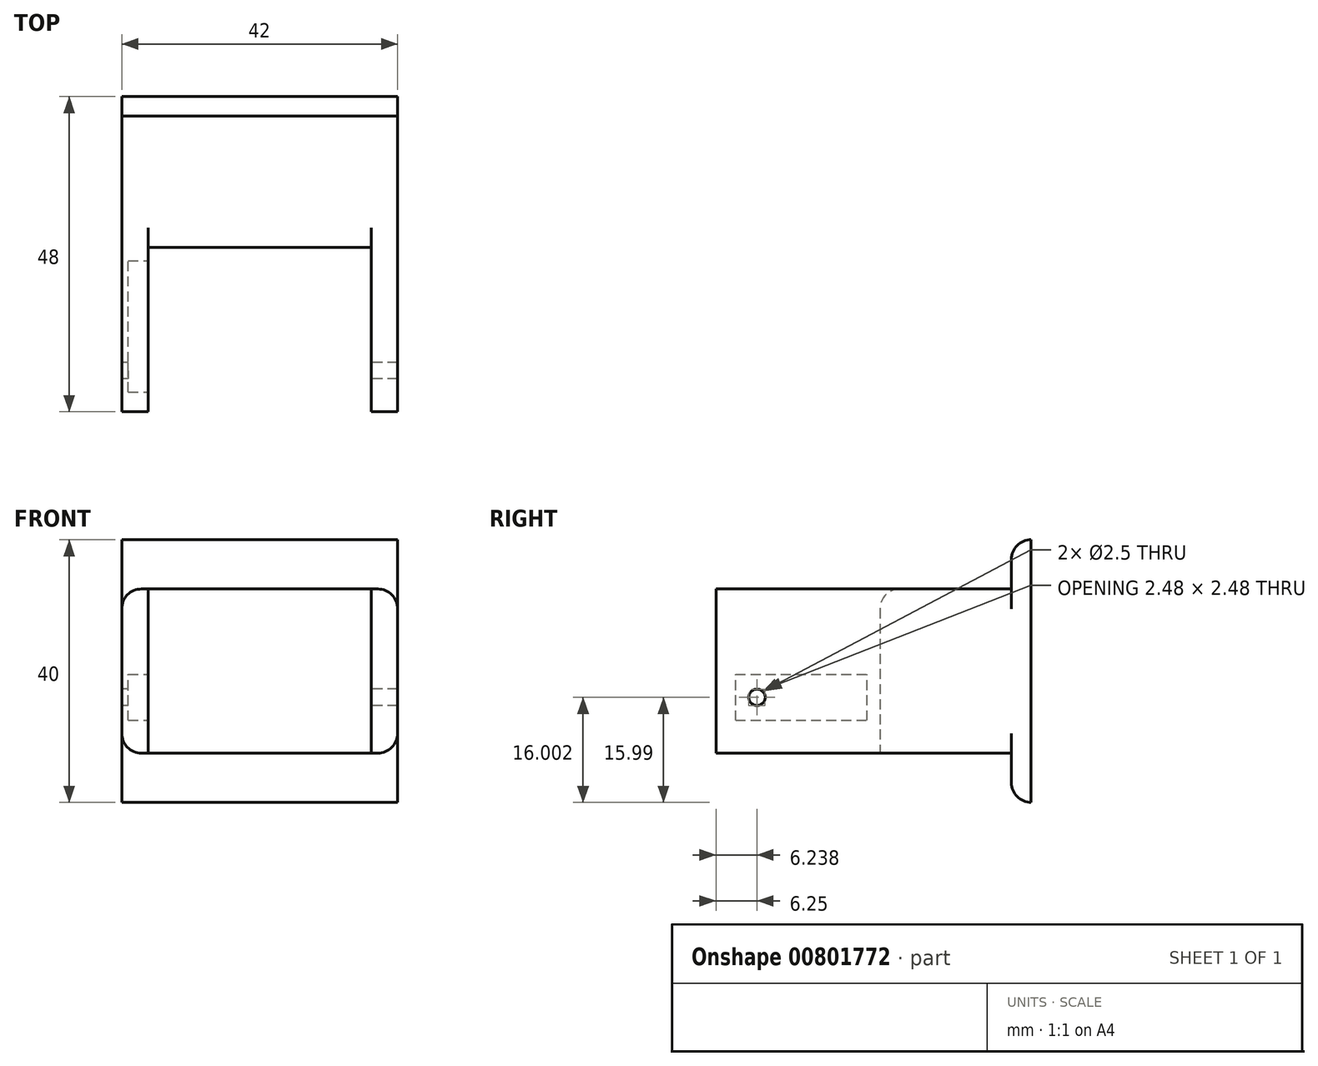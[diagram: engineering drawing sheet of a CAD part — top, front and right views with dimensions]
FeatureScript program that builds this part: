
annotation { "Feature Type Name" : "Feature", "Feature Type Description" : "" }
export const myFeature = defineFeature(function(context is Context, id is Id, definition is map)
    precondition{}
    {
        {
            var Q0;
            Q0=qCreatedBy(makeId("Front.planeOp"),FACE);
            var sketch = newSketch(context, id + "F0", { "sketchPlane" : qUnion([Q0])});
            skLineSegment(sketch, "E0.bottom", {"start": v(-23.47, 32.82) * mm, "end": v(18.53, 32.82) * mm});
            skLineSegment(sketch, "E0.top", {"start": v(-23.47, -7.18) * mm, "end": v(18.53, -7.18) * mm});
            skLineSegment(sketch, "E0.left", {"start": v(-23.47, 32.82) * mm, "end": v(-23.47, -7.18) * mm});
            skLineSegment(sketch, "E0.right", {"start": v(18.53, 32.82) * mm, "end": v(18.53, -7.18) * mm});
            skSolve(sketch);
        }
        {
            var Q0;
            Q0 = qSketchRegion(id + "F0", true);
            extrude(context, id + "F1", {"entities" : qUnion([Q0]), "depth" : 3 * mm, "offsetDistance" : 25 * mm});
        }
        {
            var Q0;
            Q0=makeQuery(id+"F1.opExtrude","CAP_FACE",FACE,{"disambiguationData":[OSD([sQuery(id+"F0.wireOp",EDGE,"E0.bottom"),sQuery(id+"F0.wireOp",EDGE,"E0.top"),sQuery(id+"F0.wireOp",EDGE,"E0.left"),sQuery(id+"F0.wireOp",EDGE,"E0.right")])],"isStart":false});
            var sketch = newSketch(context, id + "F2", { "sketchPlane" : qUnion([Q0])});
            skLineSegment(sketch, "E1.bottom", {"start": v(-23.47, 25.32) * mm, "end": v(18.53, 25.32) * mm});
            skLineSegment(sketch, "E1.top", {"start": v(-23.47, 0.32) * mm, "end": v(18.53, 0.32) * mm});
            skLineSegment(sketch, "E1.left", {"start": v(-23.47, 25.32) * mm, "end": v(-23.47, 0.32) * mm});
            skLineSegment(sketch, "E1.right", {"start": v(18.53, 25.32) * mm, "end": v(18.53, 0.32) * mm});
            skSolve(sketch);
        }
        {
            var Q0;
            Q0 = qSketchRegion(id + "F2", true);
            extrude(context, id + "F3", {"entities" : qUnion([Q0]), "operationType" : NewBodyOperationType.ADD, "depth" : 45 * mm, "offsetDistance" : 25 * mm});
        }
        {
            var Q0;
            Q0=makeQuery(id+"F3.opExtrude","SWEPT_FACE",FACE,{"disambiguationData":[OSD([sQuery(id+"F2.wireOp",EDGE,"E1.top")])]});
            var sketch = newSketch(context, id + "F4", { "sketchPlane" : qUnion([Q0])});
            skLineSegment(sketch, "E2.bottom", {"start": v(-19.47, 48) * mm, "end": v(14.53, 48) * mm});
            skLineSegment(sketch, "E2.top", {"start": v(-19.47, 23) * mm, "end": v(14.53, 23) * mm});
            skLineSegment(sketch, "E2.left", {"start": v(-19.47, 48) * mm, "end": v(-19.47, 23) * mm});
            skLineSegment(sketch, "E2.right", {"start": v(14.53, 48) * mm, "end": v(14.53, 23) * mm});
            skSolve(sketch);
        }
        {
            var Q0;
            Q0 = qSketchRegion(id + "F4", true);
            extrude(context, id + "F5", {"entities" : qUnion([Q0]), "operationType" : NewBodyOperationType.REMOVE, "endBound" : BoundingType.THROUGH_ALL, "oppositeDirection" : true, "depth" : 25 * mm, "offsetDistance" : 25 * mm});
        }
        {
            var Q0;
            Q0=makeQuery(id+"F5.boolean.opBoolean","COPY",FACE,{"derivedFrom":makeQuery(id+"F5.opExtrude","SWEPT_FACE",FACE,{"disambiguationData":[OSD([sQuery(id+"F4.wireOp",EDGE,"E2.left")])]})});
            var sketch = newSketch(context, id + "F6", { "sketchPlane" : qUnion([Q0])});
            skLineSegment(sketch, "E3.bottom", {"start": v(-45, 5.32) * mm, "end": v(-25, 5.32) * mm});
            skLineSegment(sketch, "E3.top", {"start": v(-45, 12.32) * mm, "end": v(-25, 12.32) * mm});
            skLineSegment(sketch, "E3.left", {"start": v(-45, 5.32) * mm, "end": v(-45, 12.32) * mm});
            skLineSegment(sketch, "E3.right", {"start": v(-25, 5.32) * mm, "end": v(-25, 12.32) * mm});
            skSolve(sketch);
        }
        {
            var Q0;
            Q0 = qSketchRegion(id + "F6", true);
            extrude(context, id + "F7", {"entities" : qUnion([Q0]), "operationType" : NewBodyOperationType.REMOVE, "oppositeDirection" : true, "depth" : 3 * mm, "offsetDistance" : 25 * mm});
        }
        {
            var Q0;
            Q0=makeQuery(id+"F3.boolean.opBoolean","MERGE",FACE,{"derivedFrom":[makeQuery(id+"F1.opExtrude","SWEPT_FACE",FACE,{"disambiguationData":[OSD([sQuery(id+"F0.wireOp",EDGE,"E0.left")])]}),makeQuery(id+"F3.opExtrude","SWEPT_FACE",FACE,{"disambiguationData":[OSD([sQuery(id+"F2.wireOp",EDGE,"E1.left")])]})]});
            var sketch = newSketch(context, id + "F8", { "sketchPlane" : qUnion([Q0])});
            skCircle(sketch, "E4", {"center": v(41.75, 8.82) * mm, "radius": 1.25 * mm});
            skSolve(sketch);
        }
        {
            var Q0;
            Q0 = qSketchRegion(id + "F8", true);
            extrude(context, id + "F9", {"entities" : qUnion([Q0]), "operationType" : NewBodyOperationType.REMOVE, "endBound" : BoundingType.THROUGH_ALL, "oppositeDirection" : true, "depth" : 25 * mm, "offsetDistance" : 25 * mm});
        }
        {
            var Q0;
            Q0=makeQuery(id+"F3.opExtrude","SWEPT_EDGE",EDGE,{"disambiguationData":[OSD([sQuery(id+"F0.wireOp",EDGE,"E0.left"),sQuery(id+"F2.wireOp",EDGE,"E1.top"),sQuery(id+"F2.wireOp",EDGE,"E1.left")])]});
            var Q1;
            Q1=makeQuery(id+"F3.opExtrude","SWEPT_EDGE",EDGE,{"disambiguationData":[OSD([sQuery(id+"F0.wireOp",EDGE,"E0.right"),sQuery(id+"F2.wireOp",EDGE,"E1.top"),sQuery(id+"F2.wireOp",EDGE,"E1.right")])]});
            var Q2;
            Q2=makeQuery(id+"F3.opExtrude","SWEPT_EDGE",EDGE,{"disambiguationData":[OSD([sQuery(id+"F0.wireOp",EDGE,"E0.left"),sQuery(id+"F2.wireOp",EDGE,"E1.bottom"),sQuery(id+"F2.wireOp",EDGE,"E1.left")])]});
            var Q3;
            Q3=makeQuery(id+"F3.opExtrude","SWEPT_EDGE",EDGE,{"disambiguationData":[OSD([sQuery(id+"F0.wireOp",EDGE,"E0.right"),sQuery(id+"F2.wireOp",EDGE,"E1.bottom"),sQuery(id+"F2.wireOp",EDGE,"E1.right")])]});
            var Q4;
            Q4=makeQuery(id+"F5.boolean.opBoolean","INTERSECT",EDGE,{"derivedFrom":[makeQuery(id+"F3.opExtrude","SWEPT_FACE",FACE,{"disambiguationData":[OSD([sQuery(id+"F2.wireOp",EDGE,"E1.bottom")])]}),makeQuery(id+"F5.opExtrude","SWEPT_FACE",FACE,{"disambiguationData":[OSD([sQuery(id+"F4.wireOp",EDGE,"E2.top")])]})]});
            var Q5;
            Q5=makeQuery(id+"F5.boolean.opBoolean","COPY",EDGE,{"derivedFrom":makeQuery(id+"F5.opExtrude","CAP_EDGE",EDGE,{"disambiguationData":[OSD([sQuery(id+"F4.wireOp",EDGE,"E2.top")])],"isStart":true})});
            var Q6;
            Q6=makeQuery(id+"F1.opExtrude","CAP_EDGE",EDGE,{"disambiguationData":[OSD([sQuery(id+"F0.wireOp",EDGE,"E0.top")])],"isStart":false});
            var Q7;
            Q7=makeQuery(id+"F1.opExtrude","CAP_EDGE",EDGE,{"disambiguationData":[OSD([sQuery(id+"F0.wireOp",EDGE,"E0.bottom")])],"isStart":false});
            fillet(context, id + "F10", {"entities" : qUnion([Q0, Q1, Q2, Q3, Q4, Q5, Q6, Q7]), "radius" : 3 * mm, "tangentPropagation" : true, "allowEdgeOverflow" : false});
        }
    });
